# Revit family: Valve-Transfer_Valve-KOHLER-Purist-14491B_1
name_source: partatom
category: Specialty Equipment
revit_build: Autodesk Revit 2017 (Build: 20160225_1515(x64)
units: mm (PartAtom-declared; Revit-internal decimal feet)

## family parameters
Cut with Voids When Loaded = No
Host = Face
OmniClass Number = 23.31.25.00
OmniClass Title = Toilet and Bath Specialties
Part Type = Normal
Room Calculation Point = No
Round Connector Dimension = Use Diameter
Shared = No

## types (2) — shared parameters
ADA Compliant = No
Assembly Code = C1030200
Date Modified = 05/11/2021
Default Elevation = 42"
Finish = Kohler-Metal-CP-Polished_Chrome
Height = 3 7/8"
Length = 4 3/16"
Manufacturer = KOHLER Co.
Master Format 2014 = 10 28 00
Master Format 2014 Name = Toilet, Bath, and Laundry Accessories
Material = Premium Metal Construction
Product Name = Purist
Product Page URL = https://www.kohler.co.uk
URL = https://www.kohler.co.uk
WaterSense Certified = No
Width = 3 7/8"

## per-type parameters (varying)
| type | Cross Handle | Description | Dist1 | Dist2 | Dist3 | Handle Clearance | Lever Handle | Model | Type |
| Cross Handle, CP-Polished Chrome | Yes | 3-way transfer valve, cross handle | 0" | 1 3/4" | 3 1/2" | 3 1/2" | No | 14491B-3-CP | 1 |
| Lever Handle, CP-Polished Chrome | No | 3-way transfer valve, lever handle | 1 1/4" | 0" | 0" | 3" | Yes | 14491B-4-CP | 2 |

## geometry (parser evidence)
native form markers: Sweep x4
no freeform markers — native parametric forms only
